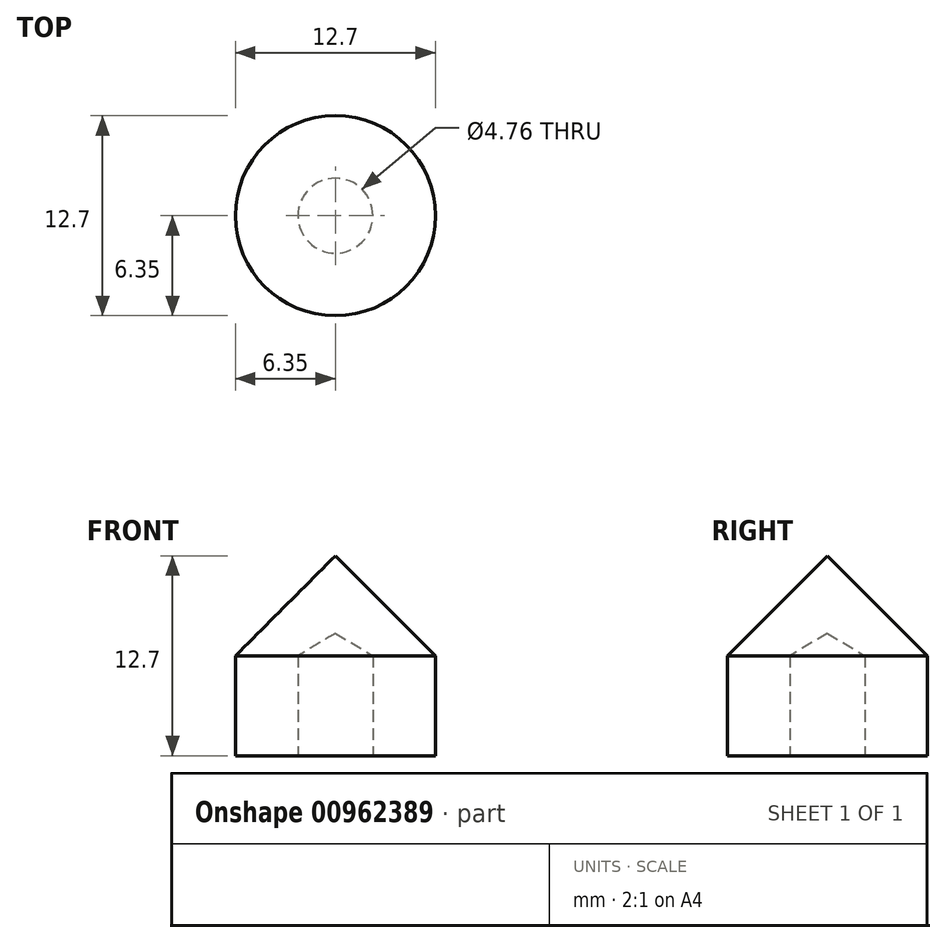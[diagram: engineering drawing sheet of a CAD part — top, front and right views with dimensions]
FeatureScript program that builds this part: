
annotation { "Feature Type Name" : "Feature", "Feature Type Description" : "" }
export const myFeature = defineFeature(function(context is Context, id is Id, definition is map)
    precondition{}
    {
        {
            var Q0;
            Q0=qCreatedBy(makeId("Right.planeOp"),FACE);
            var sketch = newSketch(context, id + "F0", { "sketchPlane" : qUnion([Q0])});
            skLineSegment(sketch, "E0", {"start": v(-6.35, 0) * mm, "end": v(-6.35, 6.35) * mm});
            skLineSegment(sketch, "E1", {"start": v(-6.35, 0) * mm, "end": v(0, 0) * mm});
            skLineSegment(sketch, "E2", {"start": v(-6.35, 6.35) * mm, "end": v(0, 12.7) * mm});
            skLineSegment(sketch, "E3", {"start": v(0, 12.7) * mm, "end": v(0, 0) * mm});
            skSolve(sketch);
        }
        {
            var Q0;
            Q0 = qSketchRegion(id + "F0", true);
            var Q1;
            Q1=sQuery(id+"F0.wireOp",EDGE,"E3");
            revolve(context, id + "F1", {"surfaceOperationType" : NewSurfaceOperationType.NEW, "entities" : qUnion([Q0]), "axis" : qUnion([Q1]), "revolveType" : RevolveType.FULL});
        }
        {
            var Q0;
            Q0=makeQuery(id+"F1.opRevolve","SWEPT_FACE",FACE,{"disambiguationData":[OSD([sQuery(id+"F0.wireOp",EDGE,"E1")])]});
            var sketch = newSketch(context, id + "F2", { "sketchPlane" : qUnion([Q0])});
            skCircle(sketch, "E4", {"center": v(0, 0) * mm, "radius": 2.38 * mm});
            skSolve(sketch);
        }
        {
            var Q0;
            Q0=sQuery(id+"F2.wireOp",VERTEX,"E4.center");
            var Q1;
            Q1=makeQuery(id+"F1.opRevolve","SWEPT_BODY",BODY,{"disambiguationData":[OSD([sQuery(id+"F0.wireOp",EDGE,"E0"),sQuery(id+"F0.wireOp",EDGE,"E1"),sQuery(id+"F0.wireOp",EDGE,"E2"),sQuery(id+"F0.wireOp",EDGE,"E3")])]});
            hole(context, id + "F3", {"style" : HoleStyle.SIMPLE, "endStyle" : HoleEndStyle.BLIND, "holeDiameter" : 4.76 * mm, "majorDiameter" : 6.35 * mm, "holeDepth" : 6.35 * mm, "isTappedThrough" : true, "tappedDepth" : 12.7 * mm, "tapClearance" : 3, "startFromSketch" : true, "locations" : qUnion([Q0]), "scope" : qUnion([Q1])});
        }
    });
